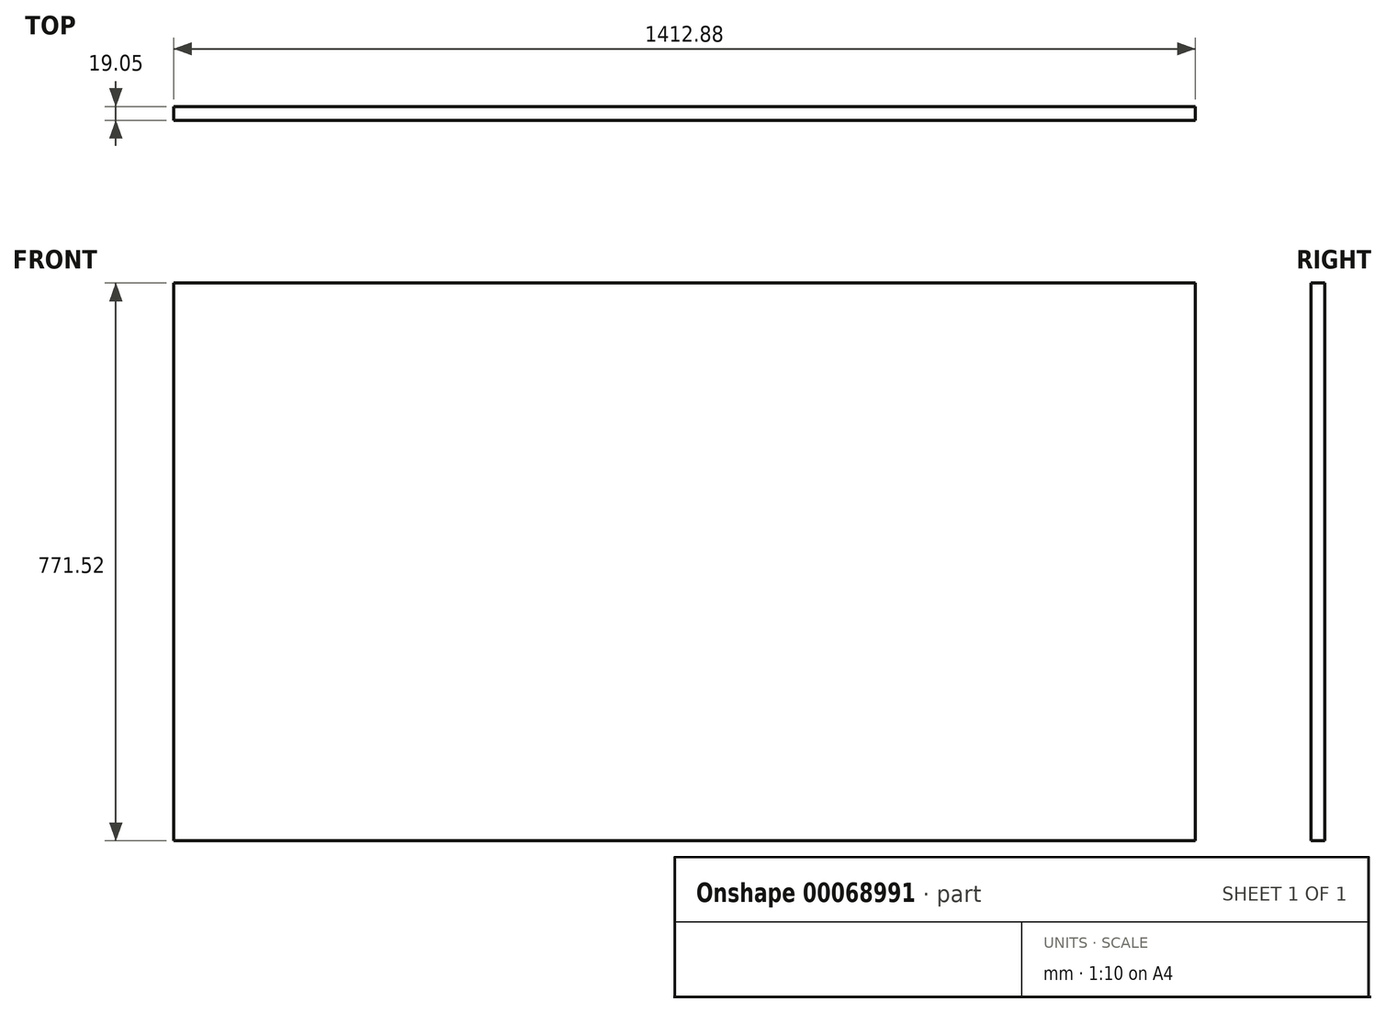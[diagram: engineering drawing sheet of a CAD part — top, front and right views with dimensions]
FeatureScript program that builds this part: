
annotation { "Feature Type Name" : "Feature", "Feature Type Description" : "" }
export const myFeature = defineFeature(function(context is Context, id is Id, definition is map)
    precondition{}
    {
        {
            var Q0;
            Q0=qCreatedBy(makeId("Front.planeOp"),FACE);
            var sketch = newSketch(context, id + "F0", { "sketchPlane" : qUnion([Q0])});
            skLineSegment(sketch, "E0.bottom", {"start": v(0, 0) * mm, "end": v(1412.87, 0) * mm});
            skLineSegment(sketch, "E0.top", {"start": v(0, 771.53) * mm, "end": v(1412.88, 771.53) * mm});
            skLineSegment(sketch, "E0.left", {"start": v(0, 0) * mm, "end": v(0, 771.53) * mm});
            skLineSegment(sketch, "E0.right", {"start": v(1412.87, 0) * mm, "end": v(1412.87, 771.53) * mm});
            skSolve(sketch);
        }
        {
            var Q0;
            Q0=makeQuery(id+"F0.imprint","IMPRINT",FACE,{"disambiguationData":[TD([[makeQuery(id+"F0.imprint","IMPRINT",EDGE,{"derivedFrom":sQuery(id+"F0.wireOp",EDGE,"E0.bottom")}),1.0]])]});
            extrude(context, id + "F1", {"entities" : qUnion([Q0]), "depth" : 19.05 * mm});
        }
    });
